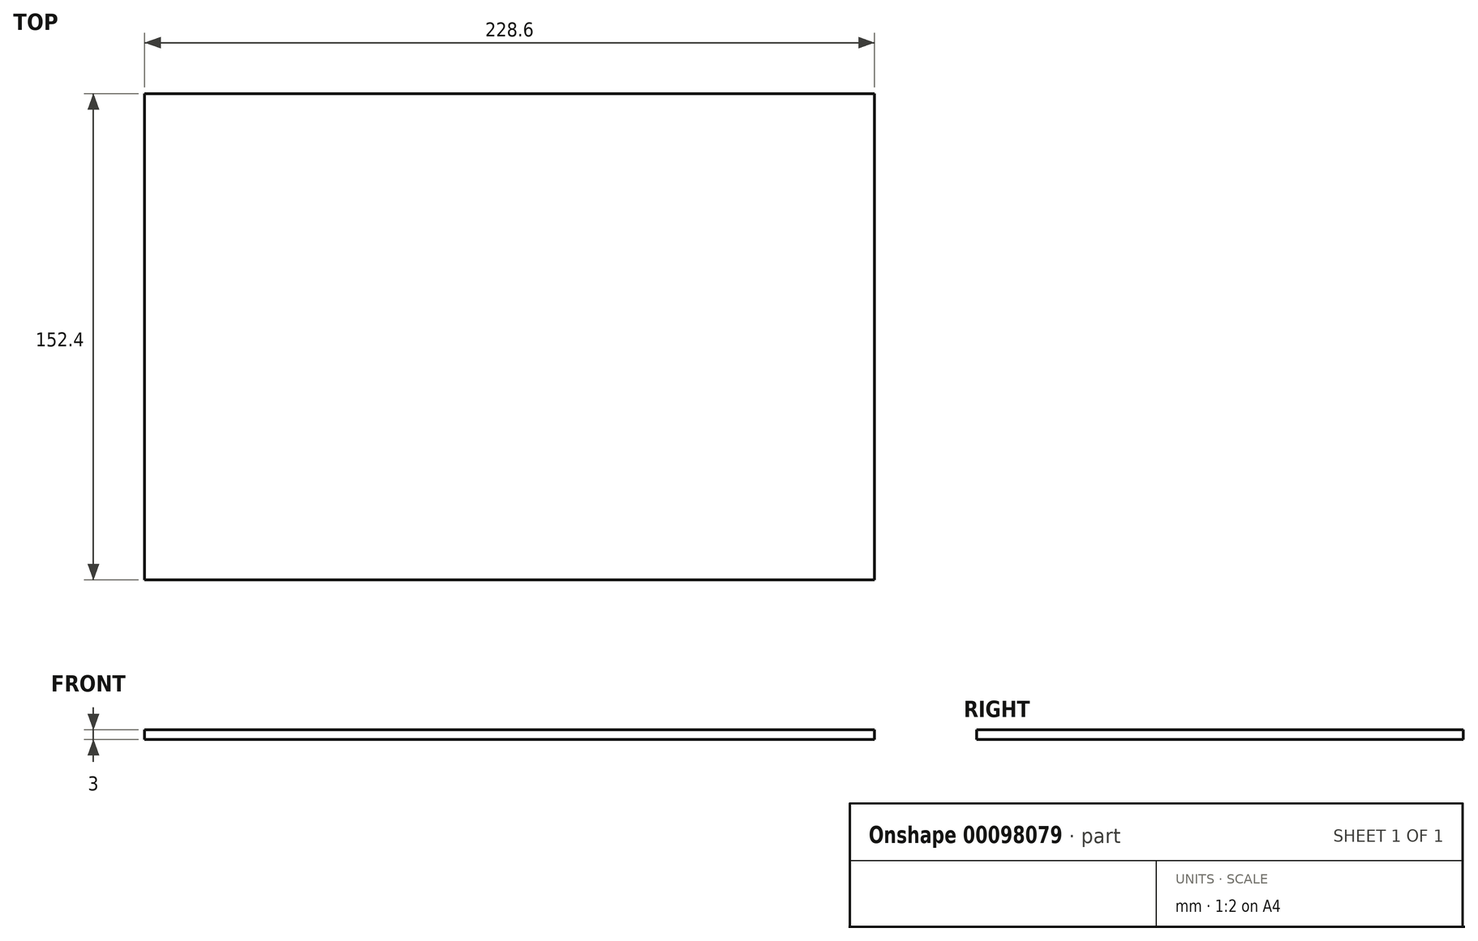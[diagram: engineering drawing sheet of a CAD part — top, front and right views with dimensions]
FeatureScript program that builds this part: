
annotation { "Feature Type Name" : "Feature", "Feature Type Description" : "" }
export const myFeature = defineFeature(function(context is Context, id is Id, definition is map)
    precondition{}
    {
        {
            assignVariable(context, id + "F0", {"name" : "Config", "anyValue" : 2});
        }
        {
            assignVariable(context, id + "F1", {"name" : "Z", "anyValue" : [1, 2, 3][getVariable(context, 'Config')]});
        }
        {
            var Q0;
            Q0=qCreatedBy(makeId("Top.planeOp"),FACE);
            var sketch = newSketch(context, id + "F2", { "sketchPlane" : qUnion([Q0])});
            skLineSegment(sketch, "E0.bottom", {"start": v(-114.3, -76.2) * mm, "end": v(114.3, -76.2) * mm});
            skLineSegment(sketch, "E0.top", {"start": v(-114.3, 76.2) * mm, "end": v(114.3, 76.2) * mm});
            skLineSegment(sketch, "E0.left", {"start": v(-114.3, -76.2) * mm, "end": v(-114.3, 76.2) * mm});
            skLineSegment(sketch, "E0.right", {"start": v(114.3, -76.2) * mm, "end": v(114.3, 76.2) * mm});
            skPoint(sketch, "E0.middle", {"position": v(0, 0) * mm});
            skSolve(sketch);
        }
        {
            var Q0;
            Q0=qSketchRegion(id+"F2",true);
            extrude(context, id + "F3", {"entities" : qUnion([Q0]), "oppositeDirection" : true, "depth" : (getVariable(context, 'Z')) * mm});
        }
    });
